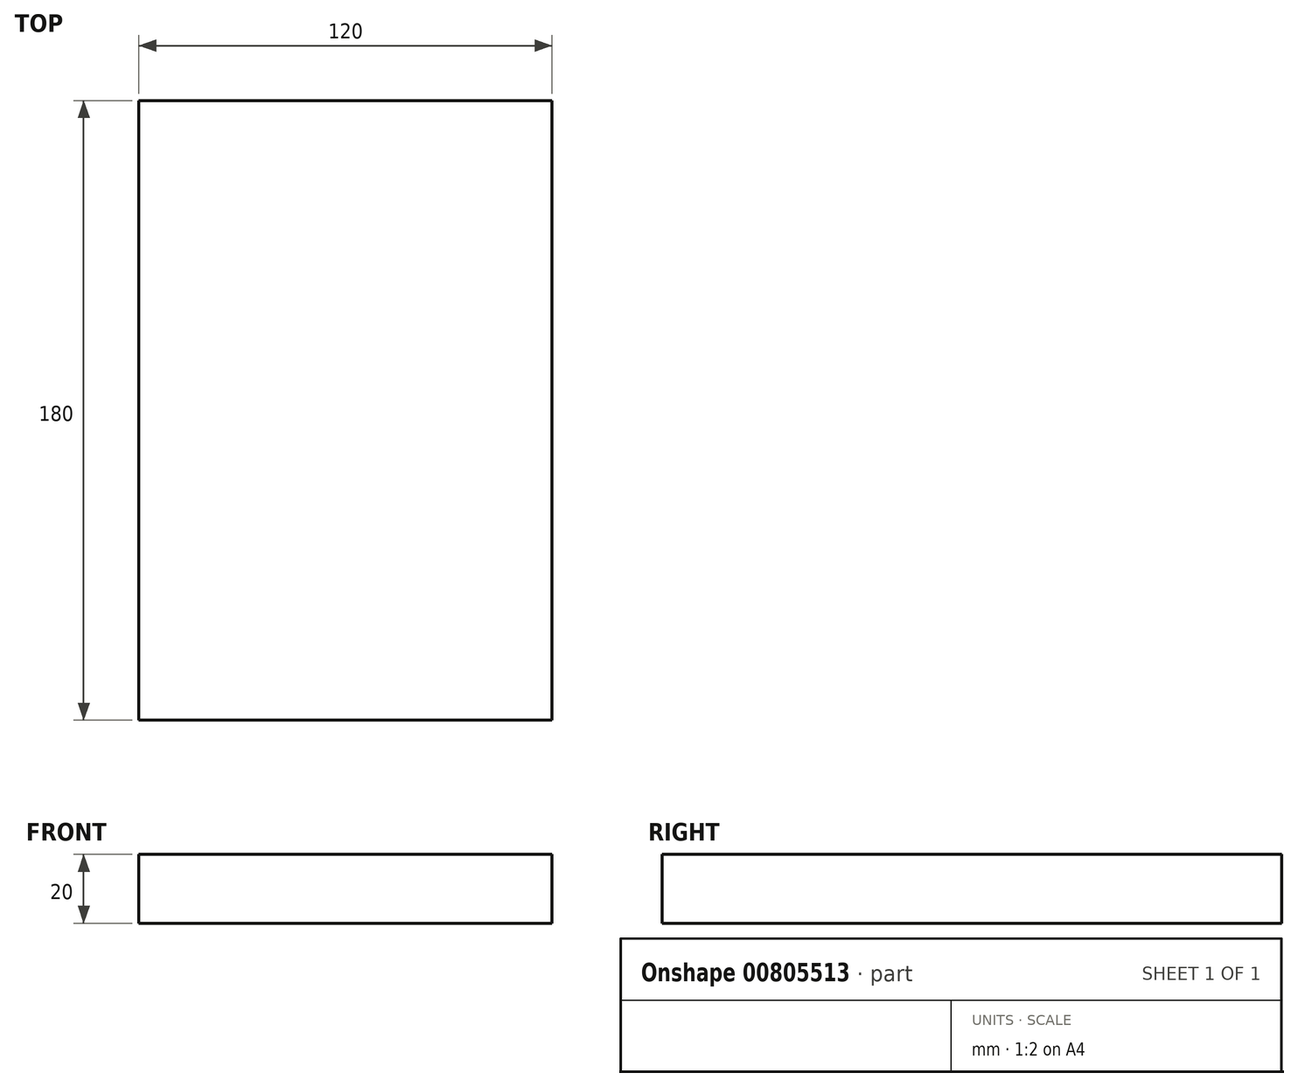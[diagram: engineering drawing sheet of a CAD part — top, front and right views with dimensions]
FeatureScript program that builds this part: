
annotation { "Feature Type Name" : "Feature", "Feature Type Description" : "" }
export const myFeature = defineFeature(function(context is Context, id is Id, definition is map)
    precondition{}
    {
        {
            var Q0;
            Q0=qCreatedBy(makeId("Top.planeOp"),FACE);
            var sketch = newSketch(context, id + "F0", { "sketchPlane" : qUnion([Q0])});
            skLineSegment(sketch, "E0.bottom", {"start": v(-62.4, 117.3) * mm, "end": v(57.6, 117.3) * mm});
            skLineSegment(sketch, "E0.top", {"start": v(-62.4, -62.7) * mm, "end": v(57.6, -62.7) * mm});
            skLineSegment(sketch, "E0.left", {"start": v(-62.4, 117.3) * mm, "end": v(-62.4, -62.7) * mm});
            skLineSegment(sketch, "E0.right", {"start": v(57.6, 117.3) * mm, "end": v(57.6, -62.7) * mm});
            skSolve(sketch);
        }
        {
            var Q0;
            Q0 = qSketchRegion(id + "F0", true);
            extrude(context, id + "F1", {"entities" : qUnion([Q0]), "depth" : 20 * mm, "offsetDistance" : 25.4 * mm});
        }
    });
